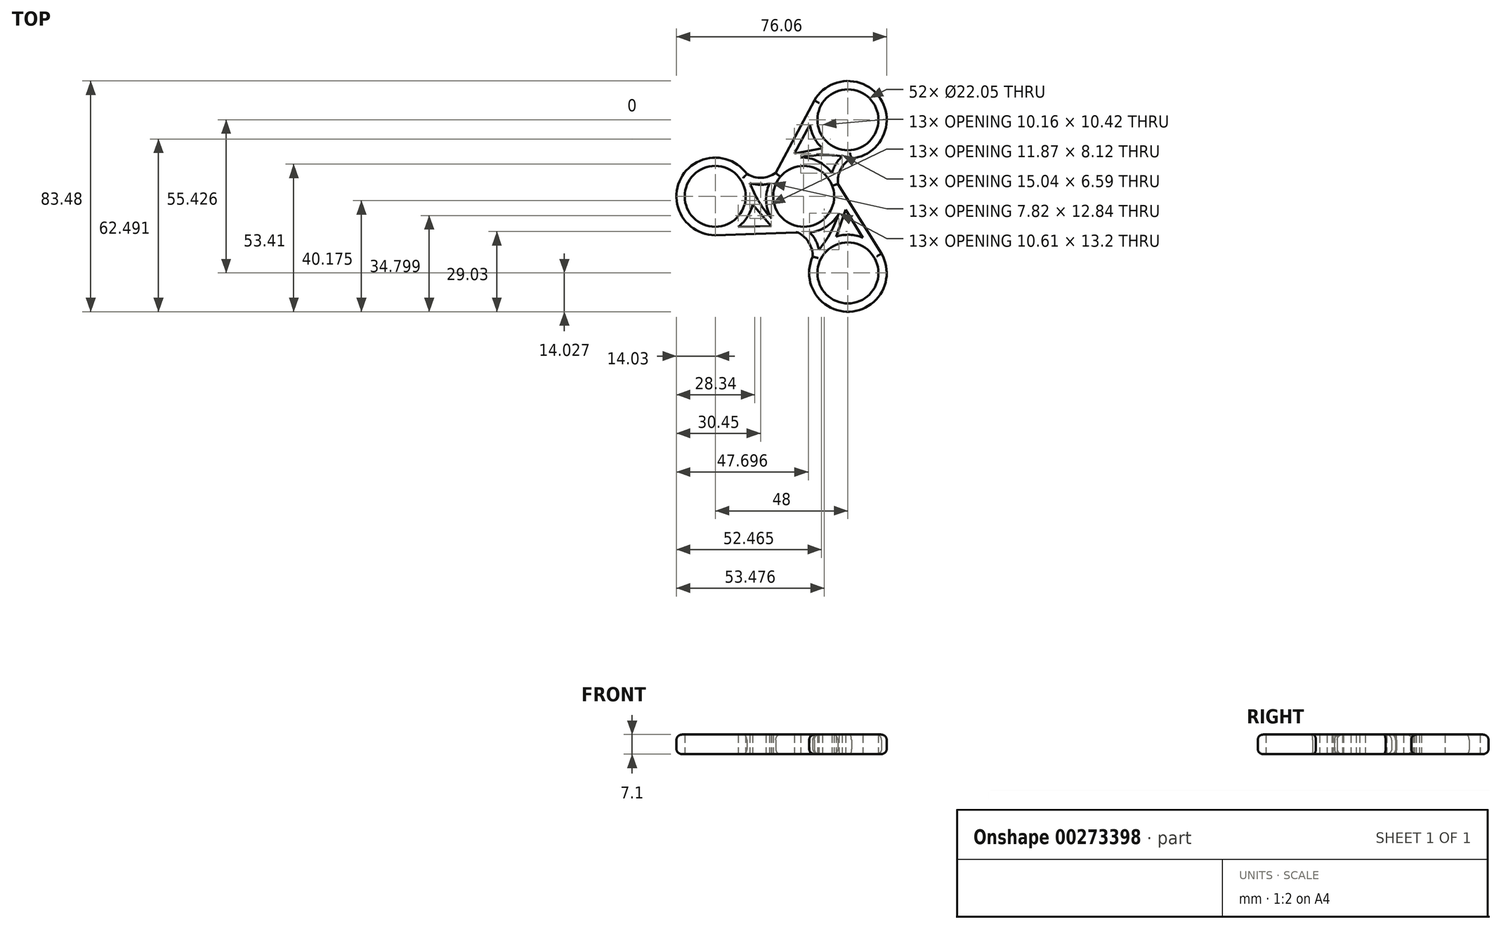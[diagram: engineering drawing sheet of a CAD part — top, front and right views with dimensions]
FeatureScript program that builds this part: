
annotation { "Feature Type Name" : "Feature", "Feature Type Description" : "" }
export const myFeature = defineFeature(function(context is Context, id is Id, definition is map)
    precondition{}
    {
        {
            var Q0;
            Q0=qCreatedBy(makeId("Top.planeOp"),FACE);
            var sketch = newSketch(context, id + "F0", { "sketchPlane" : qUnion([Q0])});
            skCircle(sketch, "E0", {"center": v(0, 0) * mm, "radius": 11.03 * mm});
            skCircle(sketch, "E1", {"center": v(16, 27.71) * mm, "radius": 11.03 * mm});
            skLineSegment(sketch, "E2", {"start": v(0, 0) * mm, "end": v(16, 27.71) * mm, "construction": true});
            skArc(sketch, "E3", {"start": v(17.28, 13.75) * mm, "mid": v(27.81, 35.27) * mm, "end": v(3.85, 34.73) * mm});
            skLineSegment(sketch, "E4", {"start": v(16, 27.71) * mm, "end": v(3.85, 34.73) * mm, "construction": true});
            skPoint(sketch, "E5.visualSharp", {"position": v(8.99, 15.57) * mm});
            skLineSegment(sketch, "E6", {"start": v(16, 27.71) * mm, "end": v(28.15, 20.7) * mm, "construction": true});
            skLineSegment(sketch, "E7", {"start": v(8, 13.86) * mm, "end": v(-1.53, 19.36) * mm, "construction": true});
            skArc(sketch, "E8", {"start": v(2.29, 25.96) * mm, "mid": v(3.75, 21.3) * mm, "end": v(6.74, 17.44) * mm});
            skLineSegment(sketch, "E9", {"start": v(12.33, 11.36) * mm, "end": v(15.11, 14.17) * mm, "construction": true});
            skLineSegment(sketch, "E10", {"start": v(12.33, 11.36) * mm, "end": v(10.43, 8.07) * mm, "construction": true});
            skCircle(sketch, "E11", {"center": v(0, 0) * mm, "radius": 13.19 * mm, "construction": true});
            skArc(sketch, "E12", {"start": v(10.22, 8.37) * mm, "mid": v(5.28, 12.63) * mm, "end": v(-1.08, 14.1) * mm});
            skPoint(sketch, "E13.center", {"position": v(-0.23, 0.06) * mm});
            skLineSegment(sketch, "E14", {"start": v(6.74, 17.44) * mm, "end": v(-3.77, 15.48) * mm});
            skPoint(sketch, "E15.orphan", {"position": v(-4.4, 14.37) * mm});
            skPoint(sketch, "E16.orphan", {"position": v(14.14, -3.77) * mm});
            skPoint(sketch, "E17.orphan", {"position": v(15.29, -4.48) * mm});
            skPoint(sketch, "E18.orphan", {"position": v(9.2, 15.94) * mm});
            skArc(sketch, "E19.1.1", {"start": v(-23.63, -11) * mm, "mid": v(-20.32, -7.4) * mm, "end": v(-18.48, -2.88) * mm});
            skLineSegment(sketch, "E19.1.2", {"start": v(-32, 0) * mm, "end": v(-32, 14.03) * mm, "construction": true});
            skPoint(sketch, "E19.1.4", {"position": v(-18.4, 0) * mm});
            skPoint(sketch, "E19.1.5", {"position": v(0.06, -0.23) * mm});
            skPoint(sketch, "E19.1.6", {"position": v(-10.25, -11) * mm});
            skCircle(sketch, "E19.1.7", {"center": v(-32, 0) * mm, "radius": 11.03 * mm});
            skLineSegment(sketch, "E19.1.8", {"start": v(-18.48, -2.88) * mm, "end": v(-11.75, -10.73) * mm});
            skLineSegment(sketch, "E19.1.9", {"start": v(-16, 0) * mm, "end": v(-16, -11) * mm, "construction": true});
            skPoint(sketch, "E19.1.10", {"position": v(-17.97, 0) * mm});
            skArc(sketch, "E19.1.12", {"start": v(-12.36, 4.67) * mm, "mid": v(-13.58, -1.75) * mm, "end": v(-11.67, -7.99) * mm});
            skArc(sketch, "E19.1.13", {"start": v(-20.54, 8.09) * mm, "mid": v(-44.45, 6.45) * mm, "end": v(-32, -14.02) * mm});
            skLineSegment(sketch, "E19.1.14", {"start": v(-32, 0) * mm, "end": v(-32, -14.02) * mm, "construction": true});
            skLineSegment(sketch, "E19.1.16", {"start": v(-16, 5) * mm, "end": v(-12.2, 5) * mm, "construction": true});
            skLineSegment(sketch, "E19.1.18", {"start": v(-16, 5) * mm, "end": v(-19.8, 6) * mm, "construction": true});
            skArc(sketch, "E19.2.1", {"start": v(21.34, -14.96) * mm, "mid": v(16.57, -13.9) * mm, "end": v(11.73, -14.56) * mm});
            skLineSegment(sketch, "E19.2.2", {"start": v(16, -27.71) * mm, "end": v(3.85, -34.73) * mm, "construction": true});
            skPoint(sketch, "E19.2.4", {"position": v(9.2, -15.94) * mm});
            skPoint(sketch, "E19.2.5", {"position": v(0.17, 0.17) * mm});
            skPoint(sketch, "E19.2.6", {"position": v(14.65, -3.37) * mm});
            skCircle(sketch, "E19.2.7", {"center": v(16, -27.71) * mm, "radius": 11.03 * mm});
            skLineSegment(sketch, "E19.2.8", {"start": v(11.73, -14.56) * mm, "end": v(15.17, -4.82) * mm});
            skLineSegment(sketch, "E19.2.9", {"start": v(8, -13.86) * mm, "end": v(17.53, -8.36) * mm, "construction": true});
            skPoint(sketch, "E19.2.10", {"position": v(8.99, -15.57) * mm});
            skArc(sketch, "E19.2.12", {"start": v(2.14, -13.04) * mm, "mid": v(8.3, -10.89) * mm, "end": v(12.75, -6.11) * mm});
            skArc(sketch, "E19.2.13", {"start": v(3.27, -21.83) * mm, "mid": v(16.64, -41.72) * mm, "end": v(28.15, -20.7) * mm});
            skLineSegment(sketch, "E19.2.14", {"start": v(16, -27.71) * mm, "end": v(28.15, -20.7) * mm, "construction": true});
            skLineSegment(sketch, "E19.2.16", {"start": v(3.67, -16.36) * mm, "end": v(1.77, -13.07) * mm, "construction": true});
            skLineSegment(sketch, "E19.2.18", {"start": v(3.67, -16.36) * mm, "end": v(4.7, -20.15) * mm, "construction": true});
            skArc(sketch, "E20", {"start": v(17.28, 13.75) * mm, "mid": v(13.46, 9.86) * mm, "end": v(12.4, 4.52) * mm});
            skLineSegment(sketch, "E21", {"start": v(12.4, 4.52) * mm, "end": v(28.15, -20.7) * mm});
            skLineSegment(sketch, "E22.1.0", {"start": v(-10.1, 8.47) * mm, "end": v(3.85, 34.73) * mm});
            skArc(sketch, "E22.1.1", {"start": v(-20.54, 8.09) * mm, "mid": v(-15.27, 6.72) * mm, "end": v(-10.1, 8.47) * mm});
            skLineSegment(sketch, "E22.2.0", {"start": v(-2.28, -13) * mm, "end": v(-32, -14.02) * mm});
            skArc(sketch, "E22.2.1", {"start": v(3.27, -21.83) * mm, "mid": v(1.81, -16.58) * mm, "end": v(-2.28, -13) * mm});
            skArc(sketch, "E23.0", {"start": v(13.95, 14.45) * mm, "mid": v(11.63, 11.7) * mm, "end": v(10.22, 8.37) * mm});
            skArc(sketch, "E24.trimOffspring", {"start": v(9.86, 4.93) * mm, "mid": v(9.88, 4.6) * mm, "end": v(9.9, 4.28) * mm});
            skLineSegment(sketch, "E25", {"start": v(2.29, 25.96) * mm, "end": v(-3.41, 15.54) * mm});
            skLineSegment(sketch, "E26.1.0", {"start": v(-23.63, -11) * mm, "end": v(-11.75, -10.73) * mm});
            skArc(sketch, "E26.1.1", {"start": v(-19.5, 4.86) * mm, "mid": v(-15.94, 4.22) * mm, "end": v(-12.36, 4.67) * mm});
            skLineSegment(sketch, "E26.2.0", {"start": v(21.34, -14.96) * mm, "end": v(15.17, -4.82) * mm});
            skArc(sketch, "E26.2.1", {"start": v(5.54, -19.3) * mm, "mid": v(4.32, -15.92) * mm, "end": v(2.14, -13.04) * mm});
            skPoint(sketch, "E27.orphan", {"position": v(-11.52, -11) * mm});
            skArc(sketch, "E28", {"start": v(13.95, 14.45) * mm, "mid": v(6.42, 14.96) * mm, "end": v(-1.08, 14.1) * mm});
            skPoint(sketch, "E29.orphan", {"position": v(-1.86, 14.06) * mm});
            skArc(sketch, "E30.1.0", {"start": v(-19.5, 4.86) * mm, "mid": v(-16.17, -1.92) * mm, "end": v(-11.67, -7.99) * mm});
            skArc(sketch, "E30.2.0", {"start": v(5.54, -19.3) * mm, "mid": v(9.75, -13.04) * mm, "end": v(12.75, -6.11) * mm});
            skPoint(sketch, "E31.orphan", {"position": v(13.07, -5.5) * mm});
            skPoint(sketch, "E32.orphan", {"position": v(-11.3, -8.57) * mm});
            skSolve(sketch);
        }
        {
            var Q0;
            Q0=makeQuery(id+"F0.imprint","IMPRINT",FACE,{"disambiguationData":[TD([[makeQuery(id+"F0.imprint","IMPRINT",EDGE,{"derivedFrom":sQuery(id+"F0.wireOp",EDGE,"ea44153e-c5e4-4200-878d-53ebf284e07f.1.0")}),-1.0]])]});
            var Q1;
            Q1=makeQuery(id+"F0.imprint","IMPRINT",FACE,{"disambiguationData":[TD([[makeQuery(id+"F0.imprint","IMPRINT",EDGE,{"derivedFrom":sQuery(id+"F0.wireOp",EDGE,"E0")}),-1.0]])]});
            var Q2;
            Q2=makeQuery(id+"F0.imprint","IMPRINT",FACE,{"disambiguationData":[TD([[makeQuery(id+"F0.imprint","IMPRINT",EDGE,{"derivedFrom":sQuery(id+"F0.wireOp",EDGE,"E1")}),-1.0]])]});
            var Q3;
            {var subQ0=sQuery(id+"F0.wireOp",EDGE,"zqQpl2xC-KShR-byGl-JfGq-b1LpVGurQPJH");Q3=makeQuery(id+"F0.imprint","IMPRINT",FACE,{"disambiguationData":[TD([[makeQuery(id+"F0.imprint","IMPRINT",EDGE,{"derivedFrom":subQ0}),-1.0]])]});}
            extrude(context, id + "F1", {"entities" : qUnion([Q0, Q1, Q2, Q3]), "depth" : 7.1 * mm});
        }
        {
            var Q0;
            Q0=makeQuery(id+"F1.opExtrude","CAP_EDGE",EDGE,{"disambiguationData":[OSD([sQuery(id+"F0.wireOp",EDGE,"E22.2.0")])],"isStart":false});
            var Q1;
            Q1=makeQuery(id+"F1.opExtrude","CAP_EDGE",EDGE,{"disambiguationData":[OSD([sQuery(id+"F0.wireOp",EDGE,"E19.1.13")])],"isStart":false});
            var Q2;
            Q2=makeQuery(id+"F1.opExtrude","CAP_EDGE",EDGE,{"disambiguationData":[OSD([sQuery(id+"F0.wireOp",EDGE,"E22.1.1")])],"isStart":false});
            var Q3;
            Q3=makeQuery(id+"F1.opExtrude","CAP_EDGE",EDGE,{"disambiguationData":[OSD([sQuery(id+"F0.wireOp",EDGE,"E22.1.0")])],"isStart":false});
            var Q4;
            Q4=makeQuery(id+"F1.opExtrude","CAP_EDGE",EDGE,{"disambiguationData":[OSD([sQuery(id+"F0.wireOp",EDGE,"E3")])],"isStart":false});
            var Q5;
            Q5=makeQuery(id+"F1.opExtrude","CAP_EDGE",EDGE,{"disambiguationData":[OSD([sQuery(id+"F0.wireOp",EDGE,"E20")])],"isStart":false});
            var Q6;
            Q6=makeQuery(id+"F1.opExtrude","CAP_EDGE",EDGE,{"disambiguationData":[OSD([sQuery(id+"F0.wireOp",EDGE,"E21")])],"isStart":false});
            var Q7;
            Q7=makeQuery(id+"F1.opExtrude","CAP_EDGE",EDGE,{"disambiguationData":[OSD([sQuery(id+"F0.wireOp",EDGE,"E22.2.1")])],"isStart":false});
            var Q8;
            Q8=makeQuery(id+"F1.opExtrude","CAP_EDGE",EDGE,{"disambiguationData":[OSD([sQuery(id+"F0.wireOp",EDGE,"E19.2.13")])],"isStart":false});
            var Q9;
            Q9=makeQuery(id+"F1.opExtrude","CAP_EDGE",EDGE,{"disambiguationData":[OSD([sQuery(id+"F0.wireOp",EDGE,"E19.1.13")])],"isStart":true});
            var Q10;
            Q10=makeQuery(id+"F1.opExtrude","CAP_EDGE",EDGE,{"disambiguationData":[OSD([sQuery(id+"F0.wireOp",EDGE,"E22.1.1")])],"isStart":true});
            var Q11;
            Q11=makeQuery(id+"F1.opExtrude","CAP_EDGE",EDGE,{"disambiguationData":[OSD([sQuery(id+"F0.wireOp",EDGE,"E22.1.0")])],"isStart":true});
            var Q12;
            Q12=makeQuery(id+"F1.opExtrude","CAP_EDGE",EDGE,{"disambiguationData":[OSD([sQuery(id+"F0.wireOp",EDGE,"E3")])],"isStart":true});
            var Q13;
            Q13=makeQuery(id+"F1.opExtrude","CAP_EDGE",EDGE,{"disambiguationData":[OSD([sQuery(id+"F0.wireOp",EDGE,"E20")])],"isStart":true});
            var Q14;
            Q14=makeQuery(id+"F1.opExtrude","CAP_EDGE",EDGE,{"disambiguationData":[OSD([sQuery(id+"F0.wireOp",EDGE,"E21")])],"isStart":true});
            var Q15;
            Q15=makeQuery(id+"F1.opExtrude","CAP_EDGE",EDGE,{"disambiguationData":[OSD([sQuery(id+"F0.wireOp",EDGE,"E22.2.1")])],"isStart":true});
            var Q16;
            Q16=makeQuery(id+"F1.opExtrude","CAP_EDGE",EDGE,{"disambiguationData":[OSD([sQuery(id+"F0.wireOp",EDGE,"E22.2.0")])],"isStart":true});
            var Q17;
            Q17=makeQuery(id+"F1.opExtrude","SWEPT_FACE",FACE,{"disambiguationData":[OSD([sQuery(id+"F0.wireOp",EDGE,"E22.2.0")])]});
            var Q18;
            Q18=makeQuery(id+"F1.opExtrude","CAP_EDGE",EDGE,{"disambiguationData":[OSD([sQuery(id+"F0.wireOp",EDGE,"E19.2.13")])],"isStart":true});
            fillet(context, id + "F2", {"entities" : qUnion([Q0, Q1, Q2, Q3, Q4, Q5, Q6, Q7, Q8, Q9, Q10, Q11, Q12, Q13, Q14, Q15, Q16, Q17, Q18]), "radius" : 2 * mm, "tangentPropagation" : true, "allowEdgeOverflow" : false});
        }
    });
